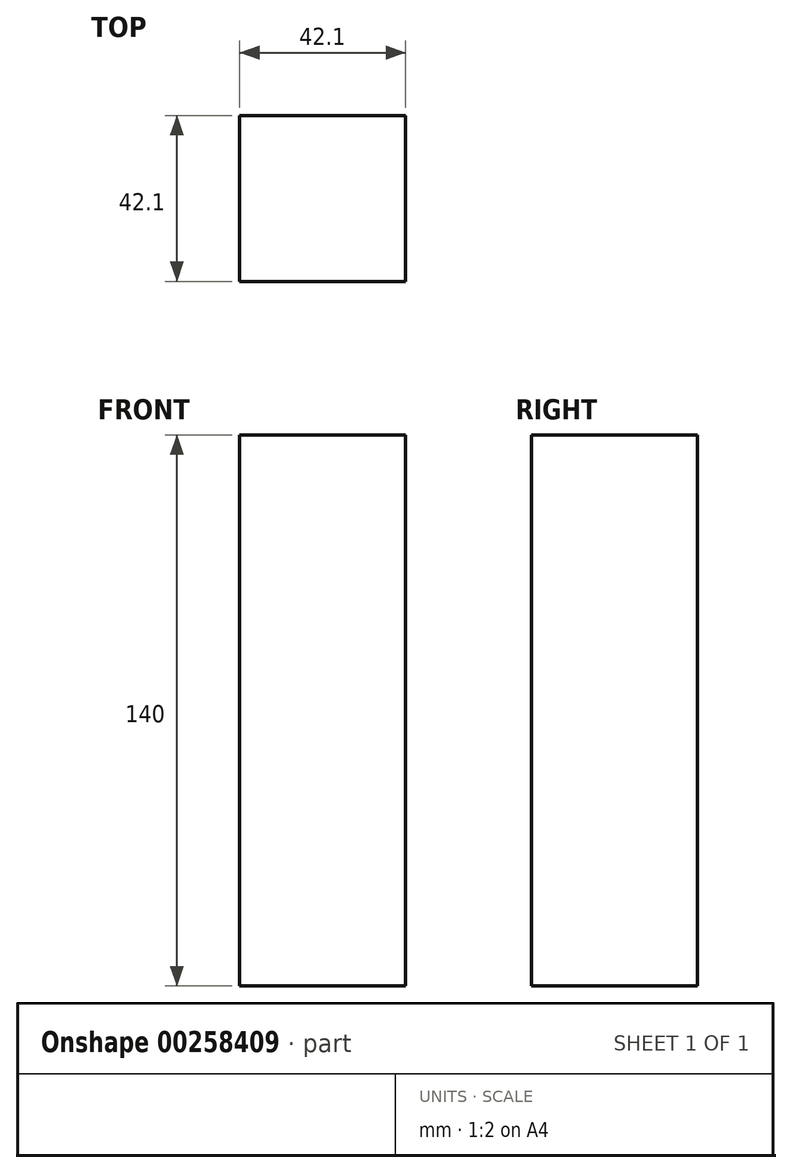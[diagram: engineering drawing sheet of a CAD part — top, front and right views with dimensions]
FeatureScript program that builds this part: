
annotation { "Feature Type Name" : "Feature", "Feature Type Description" : "" }
export const myFeature = defineFeature(function(context is Context, id is Id, definition is map)
    precondition{}
    {
        {
            var Q0;
            Q0=qCreatedBy(makeId("Top.planeOp"),FACE);
            var sketch = newSketch(context, id + "F0", { "sketchPlane" : qUnion([Q0])});
            skLineSegment(sketch, "E0.bottom", {"start": v(21.05, -21.05) * mm, "end": v(-21.05, -21.05) * mm});
            skLineSegment(sketch, "E0.top", {"start": v(21.05, 21.05) * mm, "end": v(-21.05, 21.05) * mm});
            skLineSegment(sketch, "E0.left", {"start": v(21.05, -21.05) * mm, "end": v(21.05, 21.05) * mm});
            skLineSegment(sketch, "E0.right", {"start": v(-21.05, -21.05) * mm, "end": v(-21.05, 21.05) * mm});
            skPoint(sketch, "E0.middle", {"position": v(0, 0) * mm});
            skSolve(sketch);
        }
        {
            var Q0;
            Q0=makeQuery(id+"F0.imprint","IMPRINT",FACE,{"disambiguationData":[TD([[makeQuery(id+"F0.imprint","IMPRINT",EDGE,{"derivedFrom":sQuery(id+"F0.wireOp",EDGE,"E0.bottom")}),-1.0]])]});
            extrude(context, id + "F1", {"entities" : qUnion([Q0]), "depth" : 70 * mm, "hasSecondDirection" : true, "secondDirectionOppositeDirection" : true, "secondDirectionDepth" : 70 * mm});
        }
    });
